# Revit family: 0043899
name_source: partatom
category: Lighting Fixtures
revit_build: Autodesk Revit 2016 (Build: 20150220_1215(x64)
units: mm (PartAtom-declared; Revit-internal decimal feet)

## family parameters
Cut with Voids When Loaded = No
Host = Face
Light Source = Yes
OmniClass Number = 23.80.70.00
OmniClass Title = Lighting
Part Type = Normal
Room Calculation Point = No
Round Connector Dimension = Use Diameter
Shared = No

## types (1)
- 0043899 ST Hghby HE IP66 1-10V 35000lm 840 MB
    Apparent Load = 229 VA
    Assembly Code = D5020200
    AssetType = Fixed
    ClassificationName = Uniclass2015
    ClassificationValue = EF_70_80
    Color Filter = 16777215
    Cost = 0 $
    Default Elevation = 1219 mm
    Dimming Lamp Color Temperature Shift = <None>
    DocumentationLiterature = http://www.sylvania-lighting.com
    ElectricShockClassification = Class I
    Emit Shape Visible in Rendering = No
    Emit from Circle Diameter = 298 mm
    IfcExportAs = IfcLightFixtureType
    IfcExportType = IfcLightFixtureType
    Keynote = 16500
    Lamp = LED
    LampColourRenderingIndex = 80
    LampColourTemperature = 4000 K
    LampNominalLuminous = 34500 lm
    LampsType = LED
    LuminousEfficacy = 151 lm/W
    Manufacturer = Feilo Sylvania
    ManufacturerName = Feilo Sylvania
    Material = adc12 housing
    Material_1_SYL = Body-Sylvania-START+Highbay
    Material_2_SYL = Lens-Sylvania-START+Highbay
    Material_3_SYL = <By Category>
    Material_4_SYL = <By Category>
    Model = START  Highbay HE IP66 1-10V 35000lm 840 MB
    ModelNumber = 0043899
    ModelReference = START  Highbay HE IP66 1-10V 35000lm 840 MB
    Name = START  Highbay HE IP66 1-10V 35000lm 840 MB
    NominalDepth = 365 mm
    NominalHeight = 360 mm
    NominalLength = 365 mm
    Photometric Web File = 0043899.ies
    PowerConsumption = 229 W
    PowerFactor = 0.95
    Tilt Angle = -90.00°
    Type Image = <None>
    TypeName = START  Highbay HE IP66 1-10V 35000lm 840 MB
    URL = http://www.sylvania-lighting.com
    Voltage = 230 V

## geometry (parser evidence)
native form markers: Sweep x3
no freeform markers — native parametric forms only
